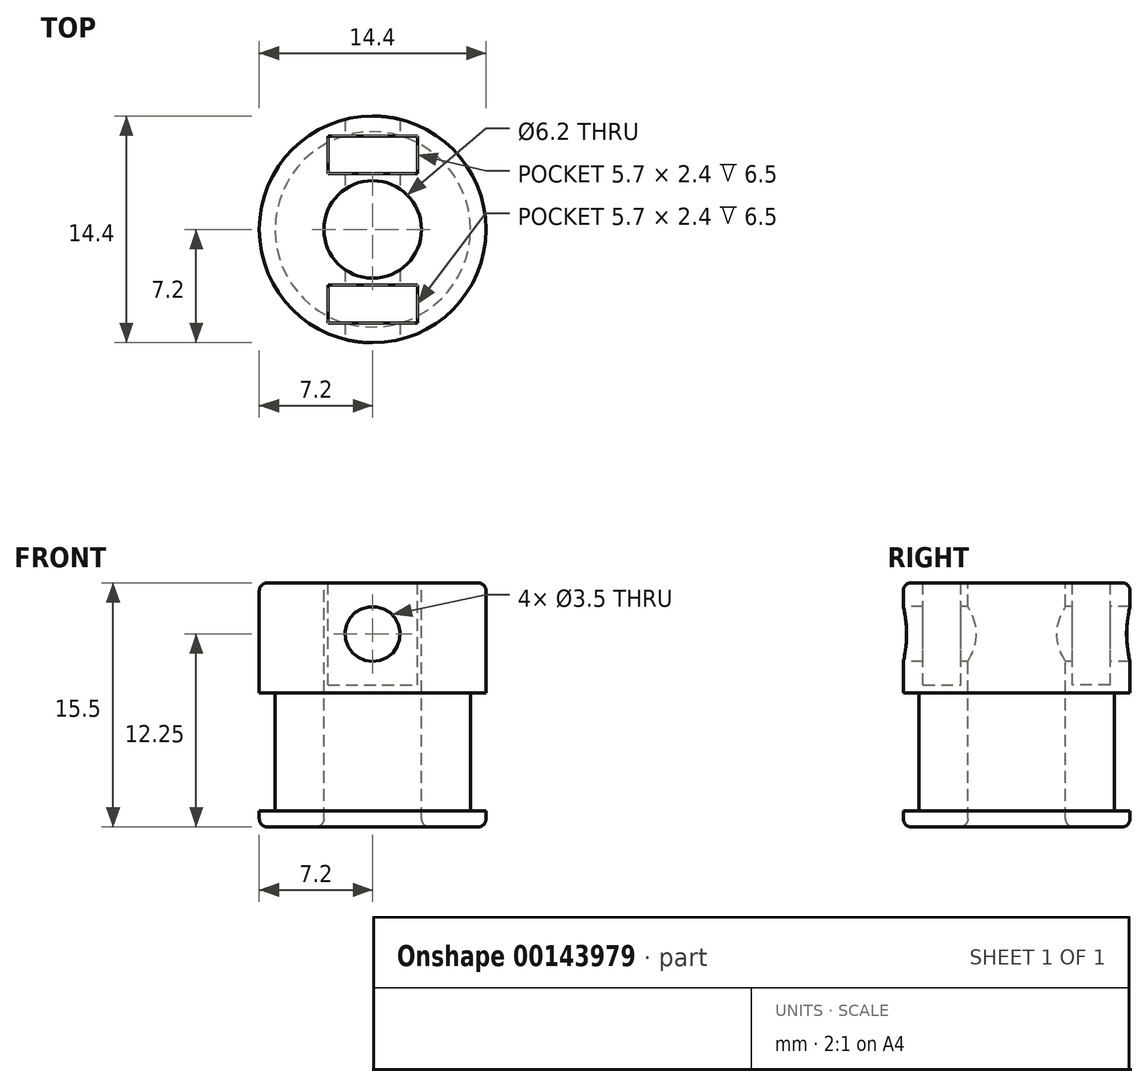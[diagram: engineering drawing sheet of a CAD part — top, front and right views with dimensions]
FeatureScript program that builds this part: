
annotation { "Feature Type Name" : "Feature", "Feature Type Description" : "" }
export const myFeature = defineFeature(function(context is Context, id is Id, definition is map)
    precondition{}
    {
        {
            var Q0;
            Q0=qCreatedBy(makeId("Front.planeOp"),FACE);
            var sketch = newSketch(context, id + "F0", { "sketchPlane" : qUnion([Q0])});
            skLineSegment(sketch, "E0", {"start": v(0, 0) * mm, "end": v(-7.2, 0) * mm});
            skLineSegment(sketch, "E1", {"start": v(-7.2, 15.5) * mm, "end": v(0, 15.5) * mm});
            skLineSegment(sketch, "E2", {"start": v(-7.2, 1) * mm, "end": v(-6.2, 1) * mm});
            skLineSegment(sketch, "E3", {"start": v(-6.2, 1) * mm, "end": v(-6.2, 8.5) * mm});
            skLineSegment(sketch, "E4", {"start": v(-6.2, 8.5) * mm, "end": v(-7.2, 8.5) * mm});
            skLineSegment(sketch, "E5", {"start": v(0, 15.5) * mm, "end": v(0, 0) * mm});
            skLineSegment(sketch, "E6", {"start": v(-3.1, 15.5) * mm, "end": v(-3.1, 0) * mm});
            skLineSegment(sketch, "E7", {"start": v(-7.2, 15.5) * mm, "end": v(-7.2, 8.5) * mm});
            skLineSegment(sketch, "E8", {"start": v(-7.2, 1) * mm, "end": v(-7.2, 0) * mm});
            skCircle(sketch, "E9", {"center": v(-7.2, 6.14) * mm, "radius": 1 * mm, "construction": true});
            skSolve(sketch);
        }
        {
            var Q0;
            {var subQ7=sQuery(id+"F0.wireOp",EDGE,"E2");Q0=makeQuery(id+"F0.imprint","IMPRINT",FACE,{"disambiguationData":[TD([[makeQuery(id+"F0.imprint","IMPRINT",EDGE,{"derivedFrom":subQ7}),-1.0]])]});}
            var Q1;
            Q1=sQuery(id+"F0.wireOp",EDGE,"E5");
            revolve(context, id + "F1", {"entities" : qUnion([Q0]), "axis" : qUnion([Q1]), "revolveType" : RevolveType.FULL});
        }
        {
            var Q0;
            Q0=makeQuery(id+"F1.opRevolve","SWEPT_FACE",FACE,{"disambiguationData":[OSD([sQuery(id+"F0.wireOp",EDGE,"E1")])]});
            var sketch = newSketch(context, id + "F2", { "sketchPlane" : qUnion([Q0])});
            skLineSegment(sketch, "E10.bottom", {"start": v(-2.85, 5.94) * mm, "end": v(2.85, 5.94) * mm});
            skLineSegment(sketch, "E10.top", {"start": v(-2.85, 3.54) * mm, "end": v(2.85, 3.54) * mm});
            skLineSegment(sketch, "E10.left", {"start": v(-2.85, 5.94) * mm, "end": v(-2.85, 3.54) * mm});
            skLineSegment(sketch, "E10.right", {"start": v(2.85, 5.94) * mm, "end": v(2.85, 3.54) * mm});
            skLineSegment(sketch, "E11.MirrorCS", {"start": v(-2.85, -5.94) * mm, "end": v(-2.85, -3.54) * mm});
            skLineSegment(sketch, "E12.MirrorCS", {"start": v(-2.85, -3.54) * mm, "end": v(2.85, -3.54) * mm});
            skLineSegment(sketch, "E13.MirrorCS", {"start": v(-2.85, -5.94) * mm, "end": v(2.85, -5.94) * mm});
            skLineSegment(sketch, "E14.MirrorCS", {"start": v(2.85, -5.94) * mm, "end": v(2.85, -3.54) * mm});
            skSolve(sketch);
        }
        {
            var Q0;
            Q0=makeQuery(id+"F2.imprint","IMPRINT",FACE,{"disambiguationData":[TD([[makeQuery(id+"F2.imprint","IMPRINT",EDGE,{"derivedFrom":sQuery(id+"F2.wireOp",EDGE,"E11.MirrorCS")}),-1.0]])]});
            var Q1;
            Q1=makeQuery(id+"F2.imprint","IMPRINT",FACE,{"disambiguationData":[TD([[makeQuery(id+"F2.imprint","IMPRINT",EDGE,{"derivedFrom":sQuery(id+"F2.wireOp",EDGE,"E10.bottom")}),-1.0]])]});
            extrude(context, id + "F3", {"entities" : qUnion([Q0, Q1]), "operationType" : NewBodyOperationType.REMOVE, "oppositeDirection" : true, "depth" : 6.5 * mm});
        }
        {
            var Q0;
            Q0=makeQuery(id+"F3.boolean.opBoolean","COPY",FACE,{"derivedFrom":makeQuery(id+"F3.opExtrude","SWEPT_FACE",FACE,{"disambiguationData":[OSD([sQuery(id+"F2.wireOp",EDGE,"E12.MirrorCS")])]})});
            var sketch = newSketch(context, id + "F4", { "sketchPlane" : qUnion([Q0])});
            skCircle(sketch, "E15", {"center": v(0, 12.25) * mm, "radius": 1.75 * mm});
            skPoint(sketch, "E15.centerSnap0", {"position": v(-2.85, 12.25) * mm});
            skSolve(sketch);
        }
        {
            var Q0;
            Q0=makeQuery(id+"F4.imprint","IMPRINT",FACE,{"disambiguationData":[TD([[makeQuery(id+"F4.imprint","IMPRINT",EDGE,{"derivedFrom":sQuery(id+"F4.wireOp",EDGE,"E15")}),1.0]])]});
            extrude(context, id + "F5", {"entities" : qUnion([Q0]), "operationType" : NewBodyOperationType.REMOVE, "endBound" : BoundingType.THROUGH_ALL, "oppositeDirection" : true, "depth" : 25 * mm, "hasSecondDirection" : true, "secondDirectionBound" : BoundingType.THROUGH_ALL, "secondDirectionOppositeDirection" : false, "secondDirectionDepth" : 25 * mm});
        }
        {
            var Q0;
            Q0=makeQuery(id+"F1.opRevolve","SWEPT_EDGE",EDGE,{"disambiguationData":[OSD([sQuery(id+"F0.wireOp",EDGE,"E0"),sQuery(id+"F0.wireOp",EDGE,"E8")])]});
            var Q1;
            Q1=makeQuery(id+"F1.opRevolve","SWEPT_EDGE",EDGE,{"disambiguationData":[OSD([sQuery(id+"F0.wireOp",EDGE,"E1"),sQuery(id+"F0.wireOp",EDGE,"E7")])]});
            var Q2;
            Q2=makeQuery(id+"F1.opRevolve","SWEPT_EDGE",EDGE,{"disambiguationData":[OSD([sQuery(id+"F0.wireOp",EDGE,"E0"),sQuery(id+"F0.wireOp",EDGE,"E6")])]});
            fillet(context, id + "F6", {"entities" : qUnion([Q0, Q1, Q2]), "radius" : 0.5 * mm, "tangentPropagation" : true, "allowEdgeOverflow" : false});
        }
    });
